# Revit family: QF_Brema_BIN200
name_source: partatom
category: Specialty Equipment
revit_build: Autodesk Revit MEP 2012 (Build: 20110916_2132(x64)
units: mm (PartAtom-declared; Revit-internal decimal feet)

## types (1)
- BIN200
    Apparent Power = 0 VA
    Assembly Code = E1090320
    BTUH = 0 W
    Cold Water Connection Height = 0 mm  [stored 0 ft]
    Cold Water Maximum Pressure = 6.0 bar
    Cold Water Minimum Pressure = 1.0 bar
    Cold Water Size = 1"
    Cold Water Size Radius = 1/2"
    Conn Conduit = Yes
    Cycle = 0 Hz
    Depth = 790 mm  [stored 2.59186 ft]
    Description = ICE STORAGE BIN
    Elec Conn Connection Height = 0 mm  [stored 0 ft]
    FL Amps = 0 A
    Height = 1000 mm  [stored 3.28084 ft]
    Indirect Waste Connection Height = 130 mm  [stored 0.426509 ft]
    Indirect Waste Radius = 1/2"
    Indirect Waste Size = 1"
    Manufacturer = BREMA
    Max Overcurrent Protection = 0 A
    Min Ckt Ampacity = 0 A
    Model = BIN200
    Phase = 0
    Refrigerant Type = R404A
    URL = www.bremaice.it
    Volts = 0 V
    Watts = 0 W
    Weight = 74 kg
    Width = 870 mm  [stored 2.85433 ft]

note: [stored X ft] marks values corroborated as IEEE doubles in the binary element streams (Revit-internal decimal feet)

## geometry (parser evidence)
native form markers: Blend x6, Sweep x2
no freeform markers — native parametric forms only
